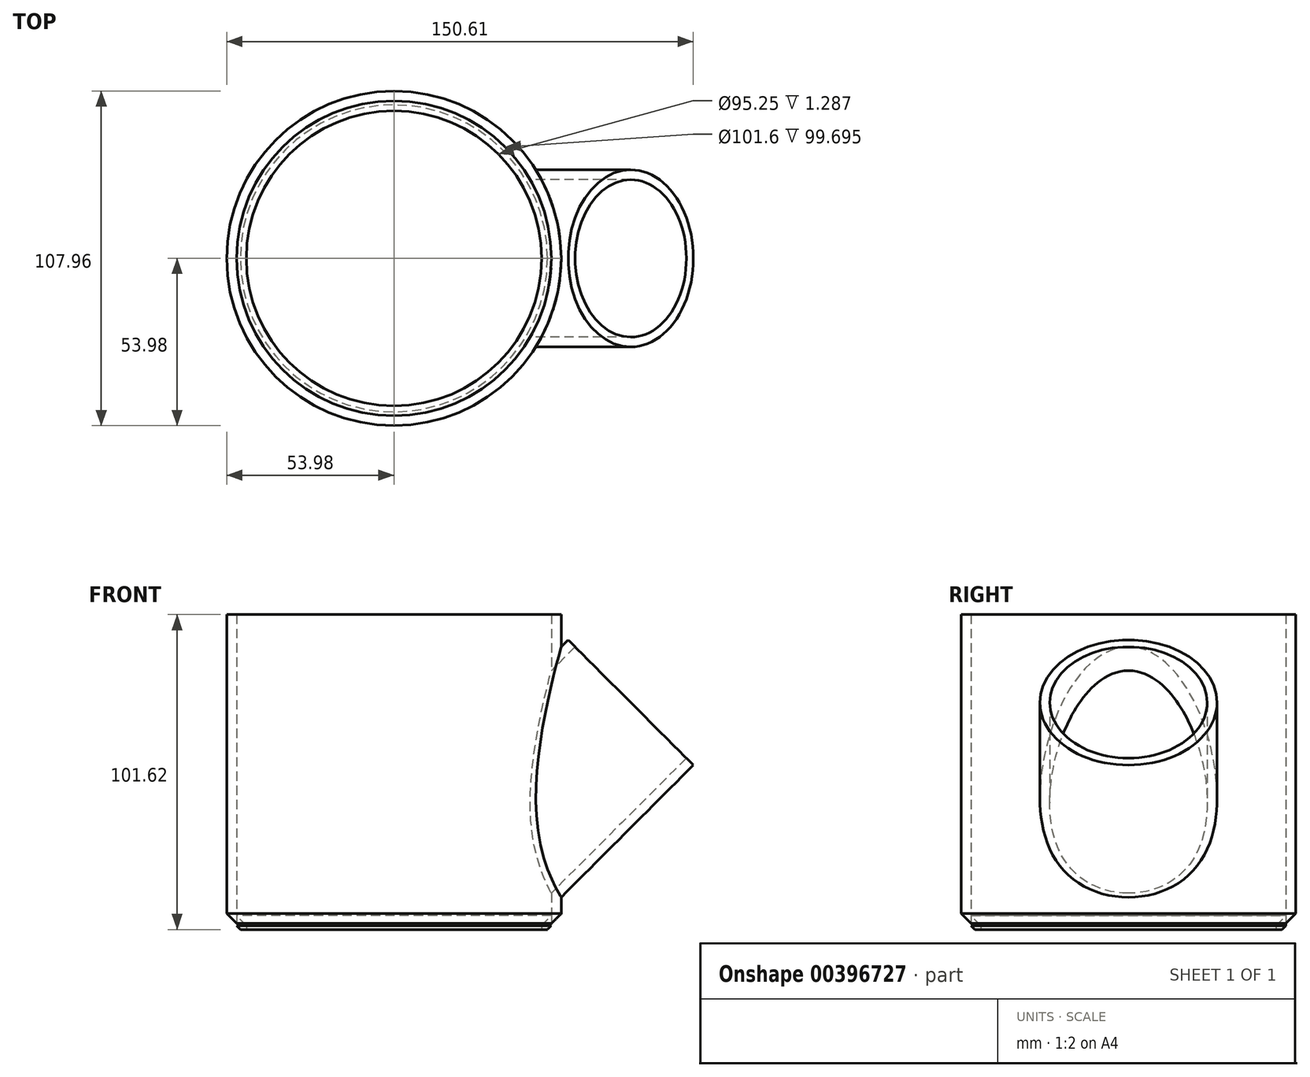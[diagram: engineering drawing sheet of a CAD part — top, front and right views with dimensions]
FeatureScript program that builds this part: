
annotation { "Feature Type Name" : "Feature", "Feature Type Description" : "" }
export const myFeature = defineFeature(function(context is Context, id is Id, definition is map)
    precondition{}
    {
        {
            var Q0;
            Q0=qCreatedBy(makeId("Top.planeOp"),FACE);
            var sketch = newSketch(context, id + "F0", { "sketchPlane" : qUnion([Q0])});
            skCircle(sketch, "E0", {"center": v(0, 0) * mm, "radius": 50.8 * mm});
            skCircle(sketch, "E1", {"center": v(0, 0) * mm, "radius": 53.98 * mm});
            skSolve(sketch);
        }
        {
            var Q0;
            Q0=qSketchRegion(id+"F0",true);
            extrude(context, id + "F1", {"entities" : qUnion([Q0]), "depth" : 101.6 * mm});
        }
        {
            var Q0;
            Q0=qCreatedBy(makeId("Top.planeOp"),FACE);
            cPlane(context, id + "F2", {"entities" : qUnion([Q0]), "cplaneType" : CPlaneType.OFFSET, "offset" : 50.8 * mm, "width" : 152.4 * mm, "height" : 152.4 * mm});
        }
        {
            var Q0;
            Q0=qCreatedBy(id+"F2.planeOp",FACE);
            var sketch = newSketch(context, id + "F3", { "sketchPlane" : qUnion([Q0])});
            skCircle(sketch, "E2.0", {"center": v(0, 0) * mm, "radius": 53.98 * mm, "construction": true});
            skLineSegment(sketch, "E3", {"start": v(0, 0) * mm, "end": v(53.98, 0) * mm, "construction": true});
            skLineSegment(sketch, "E4", {"start": v(53.98, 0) * mm, "end": v(53.98, 56) * mm});
            skSolve(sketch);
        }
        {
            var Q0;
            Q0=sQuery(id+"F3.wireOp",EDGE,"E4");
            cPlane(context, id + "F4", {"entities" : qUnion([Q0]), "cplaneType" : CPlaneType.LINE_ANGLE, "offset" : 25.4 * mm, "angle" : 45 * degree, "width" : 152.4 * mm, "height" : 152.4 * mm});
        }
        {
            var Q0;
            Q0=qCreatedBy(id+"F4.planeOp",FACE);
            var sketch = newSketch(context, id + "F5", { "sketchPlane" : qUnion([Q0])});
            skPoint(sketch, "E5.0", {"position": v(0, -2.25) * mm});
            skCircle(sketch, "E6", {"center": v(0, -2.25) * mm, "radius": 25.4 * mm});
            skCircle(sketch, "E7", {"center": v(0, -2.25) * mm, "radius": 28.58 * mm});
            skSolve(sketch);
        }
        {
            var Q0;
            Q0=makeQuery(id+"F5.imprint","IMPRINT",FACE,{"disambiguationData":[TD([[makeQuery(id+"F5.imprint","IMPRINT",EDGE,{"derivedFrom":sQuery(id+"F5.wireOp",EDGE,"E6")}),-1.0]])]});
            extrude(context, id + "F6", {"entities" : qUnion([Q0]), "operationType" : NewBodyOperationType.ADD, "depth" : 31.75 * mm, "hasSecondDirection" : true, "secondDirectionOppositeDirection" : true, "secondDirectionDepth" : 50.8 * mm});
        }
        {
            var Q0;
            Q0=makeQuery(id+"F0.imprint","IMPRINT",FACE,{"disambiguationData":[TD([[makeQuery(id+"F0.imprint","IMPRINT",EDGE,{"derivedFrom":sQuery(id+"F0.wireOp",EDGE,"E0")}),1.0]])]});
            extrude(context, id + "F7", {"entities" : qUnion([Q0]), "operationType" : NewBodyOperationType.REMOVE, "endBound" : BoundingType.THROUGH_ALL, "depth" : 271.78 * mm, "hasSecondDirection" : true, "secondDirectionBound" : BoundingType.THROUGH_ALL, "secondDirectionOppositeDirection" : true, "secondDirectionDepth" : 25.4 * mm});
        }
        {
            var Q0;
            Q0=makeQuery(id+"F5.imprint","IMPRINT",FACE,{"disambiguationData":[TD([[makeQuery(id+"F5.imprint","IMPRINT",EDGE,{"derivedFrom":sQuery(id+"F5.wireOp",EDGE,"E6")}),1.0]])]});
            extrude(context, id + "F8", {"entities" : qUnion([Q0]), "operationType" : NewBodyOperationType.REMOVE, "oppositeDirection" : true, "depth" : 50.8 * mm, "hasSecondDirection" : true, "secondDirectionBound" : BoundingType.THROUGH_ALL, "secondDirectionOppositeDirection" : false, "secondDirectionDepth" : 25.4 * mm});
        }
        {
            var Q0;
            Q0=qCreatedBy(makeId("Top.planeOp"),FACE);
            var sketch = newSketch(context, id + "F9", { "sketchPlane" : qUnion([Q0])});
            skCircle(sketch, "E8", {"center": v(0, 0) * mm, "radius": 50.8 * mm});
            skCircle(sketch, "E9.0", {"center": v(0, 0) * mm, "radius": 47.63 * mm});
            skSolve(sketch);
        }
        {
            var Q0;
            Q0 = qSketchRegion(id + "F9", true);
            extrude(context, id + "F10", {"entities" : qUnion([Q0]), "offsetDistance" : 25.4 * mm, "depth" : 6.35 * mm, "hasSecondDirection" : true, "secondDirectionOppositeDirection" : true, "secondDirectionDepth" : 7 / 406.4 * mm});
        }
        {
            var Q0;
            Q0=makeQuery(id+"F1.opExtrude","CAP_EDGE",EDGE,{"disambiguationData":[OSD([sQuery(id+"F0.wireOp",EDGE,"E0")])],"isStart":false});
            var Q1;
            Q1=makeQuery(id+"F6.opExtrude","CAP_EDGE",EDGE,{"disambiguationData":[OSD([sQuery(id+"F5.wireOp",EDGE,"E6")])],"isStart":false});
            var Q2;
            Q2=makeQuery(id+"F10.opExtrude","CAP_EDGE",EDGE,{"disambiguationData":[OSD([sQuery(id+"F9.wireOp",EDGE,"E8")])],"isStart":true});
            chamfer(context, id + "F11", {"entities" : qUnion([Q0, Q1, Q2]), "width" : 1.27 * mm, "tangentPropagation" : true});
        }
        {
            var Q0;
            Q0=makeQuery(id+"F1.opExtrude","CAP_EDGE",EDGE,{"disambiguationData":[OSD([sQuery(id+"F0.wireOp",EDGE,"E1")])],"isStart":true});
            chamfer(context, id + "F12", {"entities" : qUnion([Q0]), "width" : 5.08 * mm, "tangentPropagation" : true});
        }
        {
            var Q0;
            Q0=makeQuery(id+"F10.opExtrude","CAP_EDGE",EDGE,{"disambiguationData":[OSD([sQuery(id+"F9.wireOp",EDGE,"E9.0")])],"isStart":false});
            chamfer(context, id + "F13", {"entities" : qUnion([Q0]), "width" : 5.08 * mm, "tangentPropagation" : true});
        }
    });
